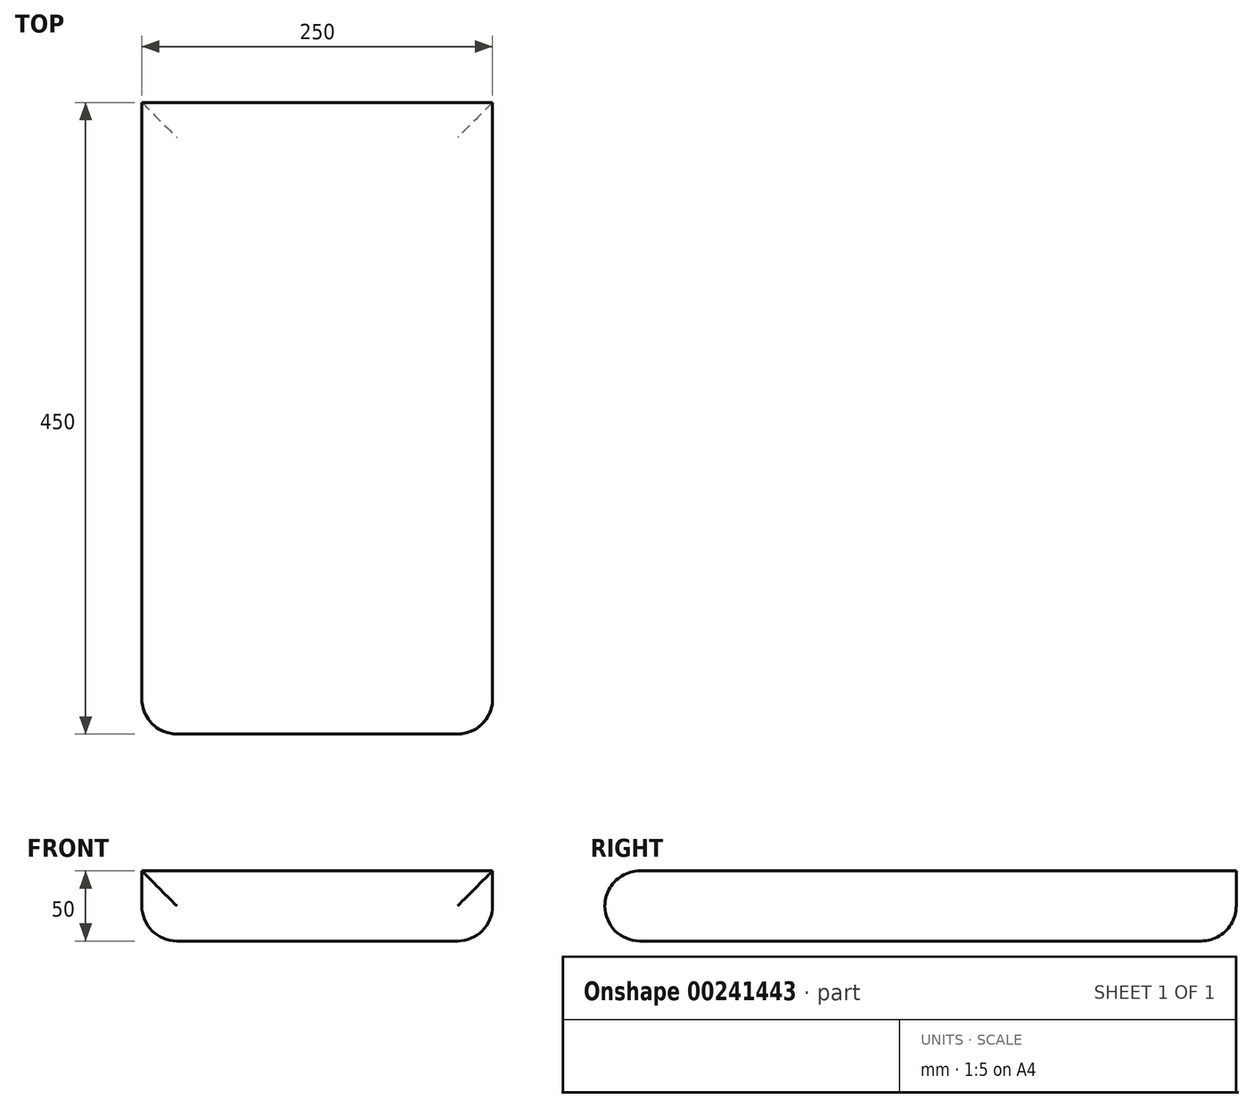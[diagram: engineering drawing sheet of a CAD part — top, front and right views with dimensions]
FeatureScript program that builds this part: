
annotation { "Feature Type Name" : "Feature", "Feature Type Description" : "" }
export const myFeature = defineFeature(function(context is Context, id is Id, definition is map)
    precondition{}
    {
        {
            var Q0;
            Q0=qCreatedBy(makeId("Top.planeOp"),FACE);
            var sketch = newSketch(context, id + "F0", { "sketchPlane" : qUnion([Q0])});
            skLineSegment(sketch, "E0.bottom", {"start": v(-125, 225) * mm, "end": v(125, 225) * mm});
            skLineSegment(sketch, "E0.top", {"start": v(-125, -225) * mm, "end": v(125, -225) * mm});
            skLineSegment(sketch, "E0.left", {"start": v(-125, 225) * mm, "end": v(-125, -225) * mm});
            skLineSegment(sketch, "E0.right", {"start": v(125, 225) * mm, "end": v(125, -225) * mm});
            skPoint(sketch, "E0.middle", {"position": v(0, 0) * mm});
            skSolve(sketch);
        }
        {
            var Q0;
            Q0 = qSketchRegion(id + "F0", true);
            extrude(context, id + "F1", {"entities" : qUnion([Q0]), "depth" : 50 * mm});
        }
        {
            var Q0;
            Q0=makeQuery(id+"F1.opExtrude","SWEPT_FACE",FACE,{"disambiguationData":[OSD([sQuery(id+"F0.wireOp",EDGE,"E0.top")])]});
            fillet(context, id + "F2", {"entities" : qUnion([Q0]), "radius" : 25 * mm, "tangentPropagation" : true, "allowEdgeOverflow" : false});
        }
        {
            var Q0;
            Q0=makeQuery(id+"F1.opExtrude","CAP_FACE",FACE,{"disambiguationData":[OSD([sQuery(id+"F0.wireOp",EDGE,"E0.bottom"),sQuery(id+"F0.wireOp",EDGE,"E0.top"),sQuery(id+"F0.wireOp",EDGE,"E0.left"),sQuery(id+"F0.wireOp",EDGE,"E0.right")])],"isStart":true});
            fillet(context, id + "F3", {"entities" : qUnion([Q0]), "radius" : 25 * mm, "tangentPropagation" : true, "allowEdgeOverflow" : false});
        }
    });
